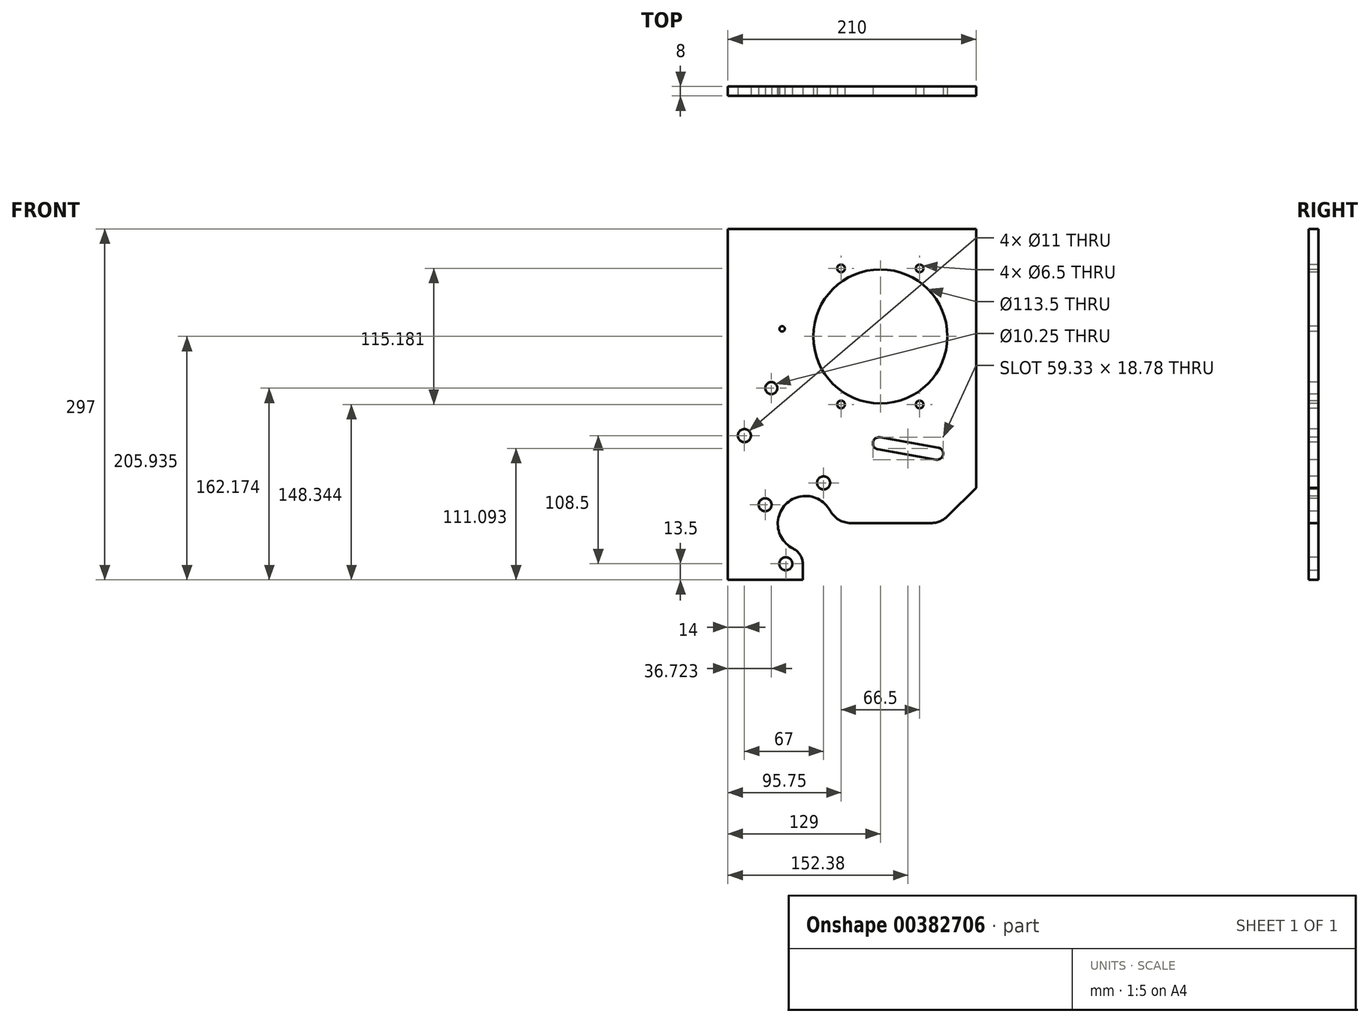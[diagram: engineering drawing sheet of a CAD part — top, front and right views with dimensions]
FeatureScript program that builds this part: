
annotation { "Feature Type Name" : "Feature", "Feature Type Description" : "" }
export const myFeature = defineFeature(function(context is Context, id is Id, definition is map)
    precondition{}
    {
        {
            var Q0;
            Q0=qCreatedBy(makeId("Front.planeOp"),FACE);
            var sketch = newSketch(context, id + "F0", { "sketchPlane" : qUnion([Q0])});
            skLineSegment(sketch, "E0.bottom", {"start": v(0, 0) * mm, "end": v(210, 0) * mm});
            skLineSegment(sketch, "E0.top", {"start": v(0, 297) * mm, "end": v(210, 297) * mm});
            skLineSegment(sketch, "E0.left", {"start": v(0, 0) * mm, "end": v(0, 297) * mm});
            skLineSegment(sketch, "E0.right", {"start": v(210, 0) * mm, "end": v(210, 297) * mm});
            skSolve(sketch);
        }
        {
            var Q0;
            Q0 = qSketchRegion(id + "F0", true);
            extrude(context, id + "F1", {"entities" : qUnion([Q0]), "oppositeDirection" : true, "depth" : 8 * mm});
        }
        {
            var Q0;
            Q0=makeQuery(id+"F1.opExtrude","CAP_FACE",FACE,{"disambiguationData":[OSD([sQuery(id+"F0.wireOp",EDGE,"E0.bottom"),sQuery(id+"F0.wireOp",EDGE,"E0.top"),sQuery(id+"F0.wireOp",EDGE,"E0.left"),sQuery(id+"F0.wireOp",EDGE,"E0.right")])],"isStart":true});
            var sketch = newSketch(context, id + "F2", { "sketchPlane" : qUnion([Q0])});
            skCircle(sketch, "E1", {"center": v(14, 122) * mm, "radius": 5.5 * mm});
            skCircle(sketch, "E2", {"center": v(31.5, 63.5) * mm, "radius": 5.5 * mm});
            skCircle(sketch, "E3", {"center": v(81, 82) * mm, "radius": 5.5 * mm});
            skCircle(sketch, "E4", {"center": v(49, 13.5) * mm, "radius": 5.5 * mm});
            skArc(sketch, "E5", {"start": v(86.42, 58.54) * mm, "mid": v(48.81, 63.74) * mm, "end": v(55.33, 26.34) * mm});
            skCircle(sketch, "E6", {"center": v(65.72, 47.41) * mm, "radius": 37.81 * mm, "construction": true});
            skLineSegment(sketch, "E7", {"start": v(49, 13.5) * mm, "end": v(81, 82) * mm, "construction": true});
            skLineSegment(sketch, "E8", {"start": v(65.72, 47.41) * mm, "end": v(31.5, 63.5) * mm, "construction": true});
            skArc(sketch, "E9", {"start": v(63.31, 13.5) * mm, "mid": v(61.07, 21.19) * mm, "end": v(55.06, 26.47) * mm});
            skLineSegment(sketch, "E10", {"start": v(63.31, 13.5) * mm, "end": v(63.31, 0) * mm});
            skLineSegment(sketch, "E11", {"start": v(104.04, 48) * mm, "end": v(171.83, 48) * mm});
            skLineSegment(sketch, "E12", {"start": v(185.97, 53.86) * mm, "end": v(210, 77.89) * mm});
            skLineSegment(sketch, "E13", {"start": v(210, 77.89) * mm, "end": v(210, 0) * mm});
            skLineSegment(sketch, "E14", {"start": v(210, 0) * mm, "end": v(63.31, 0) * mm});
            skPoint(sketch, "E15.visualSharp", {"position": v(89.21, 48) * mm});
            skArc(sketch, "E15.filletArc", {"start": v(86.42, 58.54) * mm, "mid": v(93.78, 50.83) * mm, "end": v(104.04, 48) * mm});
            skPoint(sketch, "E16.visualSharp", {"position": v(180.11, 48) * mm});
            skArc(sketch, "E16.filletArc", {"start": v(171.83, 48) * mm, "mid": v(179.48, 49.52) * mm, "end": v(185.97, 53.86) * mm});
            skSolve(sketch);
        }
        {
            var Q0;
            Q0 = qSketchRegion(id + "F2", true);
            extrude(context, id + "F3", {"entities" : qUnion([Q0]), "operationType" : NewBodyOperationType.REMOVE, "endBound" : BoundingType.THROUGH_ALL, "oppositeDirection" : true, "depth" : 25 * mm});
        }
        {
            var Q0;
            Q0=makeQuery(id+"F1.opExtrude","CAP_FACE",FACE,{"disambiguationData":[OSD([sQuery(id+"F0.wireOp",EDGE,"E0.bottom"),sQuery(id+"F0.wireOp",EDGE,"E0.top"),sQuery(id+"F0.wireOp",EDGE,"E0.left"),sQuery(id+"F0.wireOp",EDGE,"E0.right")])],"isStart":true});
            var sketch = newSketch(context, id + "F4", { "sketchPlane" : qUnion([Q0])});
            skCircle(sketch, "E17", {"center": v(129, 205.93) * mm, "radius": 56.75 * mm});
            skCircle(sketch, "E18", {"center": v(129, 205.93) * mm, "radius": 66.5 * mm, "construction": true});
            skLineSegment(sketch, "E19", {"start": v(69.98, 308.16) * mm, "end": v(175.22, 125.87) * mm, "construction": true});
            skLineSegment(sketch, "E20", {"start": v(173.2, 282.5) * mm, "end": v(82.4, 125.22) * mm, "construction": true});
            skLineSegment(sketch, "E21", {"start": v(32.69, 205.93) * mm, "end": v(217.65, 205.93) * mm, "construction": true});
            skCircle(sketch, "E22", {"center": v(95.75, 263.53) * mm, "radius": 3.25 * mm});
            skCircle(sketch, "E23", {"center": v(162.25, 263.53) * mm, "radius": 3.25 * mm});
            skCircle(sketch, "E24", {"center": v(95.75, 148.34) * mm, "radius": 3.25 * mm});
            skCircle(sketch, "E25", {"center": v(162.25, 148.34) * mm, "radius": 3.25 * mm});
            skSolve(sketch);
        }
        {
            var Q0;
            Q0 = qSketchRegion(id + "F4", true);
            extrude(context, id + "F5", {"entities" : qUnion([Q0]), "operationType" : NewBodyOperationType.REMOVE, "endBound" : BoundingType.THROUGH_ALL, "oppositeDirection" : true, "depth" : 25 * mm});
        }
        {
            var Q0;
            Q0=makeQuery(id+"F1.opExtrude","CAP_FACE",FACE,{"disambiguationData":[OSD([sQuery(id+"F0.wireOp",EDGE,"E0.bottom"),sQuery(id+"F0.wireOp",EDGE,"E0.top"),sQuery(id+"F0.wireOp",EDGE,"E0.left"),sQuery(id+"F0.wireOp",EDGE,"E0.right")])],"isStart":true});
            var sketch = newSketch(context, id + "F6", { "sketchPlane" : qUnion([Q0])});
            skCircle(sketch, "E26", {"center": v(129, 205.93) * mm, "radius": 55 * mm, "construction": true});
            skCircle(sketch, "E27", {"center": v(65.72, 47.41) * mm, "radius": 65 * mm, "construction": true});
            skLineSegment(sketch, "E28", {"start": v(93.63, 137.93) * mm, "end": v(164.37, 137.93) * mm, "construction": true});
            skLineSegment(sketch, "E29", {"start": v(172.05, 142.8) * mm, "end": v(202, 205.93) * mm, "construction": true});
            skLineSegment(sketch, "E30", {"start": v(202, 205.93) * mm, "end": v(171.65, 269.93) * mm, "construction": true});
            skLineSegment(sketch, "E31", {"start": v(171.65, 269.93) * mm, "end": v(86.35, 269.93) * mm, "construction": true});
            skLineSegment(sketch, "E32", {"start": v(86.35, 269.93) * mm, "end": v(56, 205.93) * mm, "construction": true});
            skLineSegment(sketch, "E33", {"start": v(56, 205.93) * mm, "end": v(85.95, 142.8) * mm, "construction": true});
            skLineSegment(sketch, "E34", {"start": v(56, 205.93) * mm, "end": v(202, 205.93) * mm, "construction": true});
            skPoint(sketch, "E35.visualSharp", {"position": v(88.25, 137.93) * mm});
            skArc(sketch, "E35.filletArc", {"start": v(85.95, 142.8) * mm, "mid": v(89.08, 139.25) * mm, "end": v(93.63, 137.93) * mm, "construction": true});
            skPoint(sketch, "E36.visualSharp", {"position": v(169.75, 137.93) * mm});
            skArc(sketch, "E36.filletArc", {"start": v(164.37, 137.93) * mm, "mid": v(168.92, 139.25) * mm, "end": v(172.05, 142.8) * mm, "construction": true});
            skCircle(sketch, "E37", {"center": v(127.76, 115.43) * mm, "radius": 26 * mm, "construction": true});
            skCircle(sketch, "E38", {"center": v(177, 106.75) * mm, "radius": 26 * mm, "construction": true});
            skLineSegment(sketch, "E39", {"start": v(132.27, 141.04) * mm, "end": v(181.51, 132.36) * mm, "construction": true});
            skLineSegment(sketch, "E40", {"start": v(127.76, 115.43) * mm, "end": v(177, 106.75) * mm, "construction": true});
            skLineSegment(sketch, "E41", {"start": v(123.24, 89.83) * mm, "end": v(172.49, 81.15) * mm, "construction": true});
            skArc(sketch, "E42", {"start": v(128.65, 120.48) * mm, "mid": v(122.71, 116.32) * mm, "end": v(126.87, 110.39) * mm});
            skArc(sketch, "E43", {"start": v(176.11, 101.7) * mm, "mid": v(182.05, 105.86) * mm, "end": v(177.89, 111.8) * mm});
            skLineSegment(sketch, "E44", {"start": v(128.65, 120.48) * mm, "end": v(177.89, 111.8) * mm});
            skLineSegment(sketch, "E45", {"start": v(176.11, 101.7) * mm, "end": v(126.87, 110.39) * mm});
            skCircle(sketch, "E46", {"center": v(36.72, 162.17) * mm, "radius": 26 * mm, "construction": true});
            skCircle(sketch, "E47", {"center": v(36.72, 162.17) * mm, "radius": 5.12 * mm});
            skCircle(sketch, "E48", {"center": v(45.9, 212.34) * mm, "radius": 2.25 * mm});
            skLineSegment(sketch, "E49", {"start": v(6.87, 75) * mm, "end": v(79.2, 229.28) * mm, "construction": true});
            skLineSegment(sketch, "E50.bottom", {"start": v(116.5, 121.5) * mm, "end": v(141.5, 121.5) * mm, "construction": true});
            skLineSegment(sketch, "E50.top", {"start": v(116.5, 47.19) * mm, "end": v(141.5, 47.19) * mm, "construction": true});
            skLineSegment(sketch, "E50.left", {"start": v(116.5, 121.5) * mm, "end": v(116.5, 47.19) * mm, "construction": true});
            skLineSegment(sketch, "E50.right", {"start": v(141.5, 121.5) * mm, "end": v(141.5, 47.19) * mm, "construction": true});
            skSolve(sketch);
        }
        {
            var Q0;
            Q0 = qSketchRegion(id + "F6", true);
            extrude(context, id + "F7", {"entities" : qUnion([Q0]), "operationType" : NewBodyOperationType.REMOVE, "endBound" : BoundingType.THROUGH_ALL, "oppositeDirection" : true, "depth" : 25 * mm});
        }
    });
